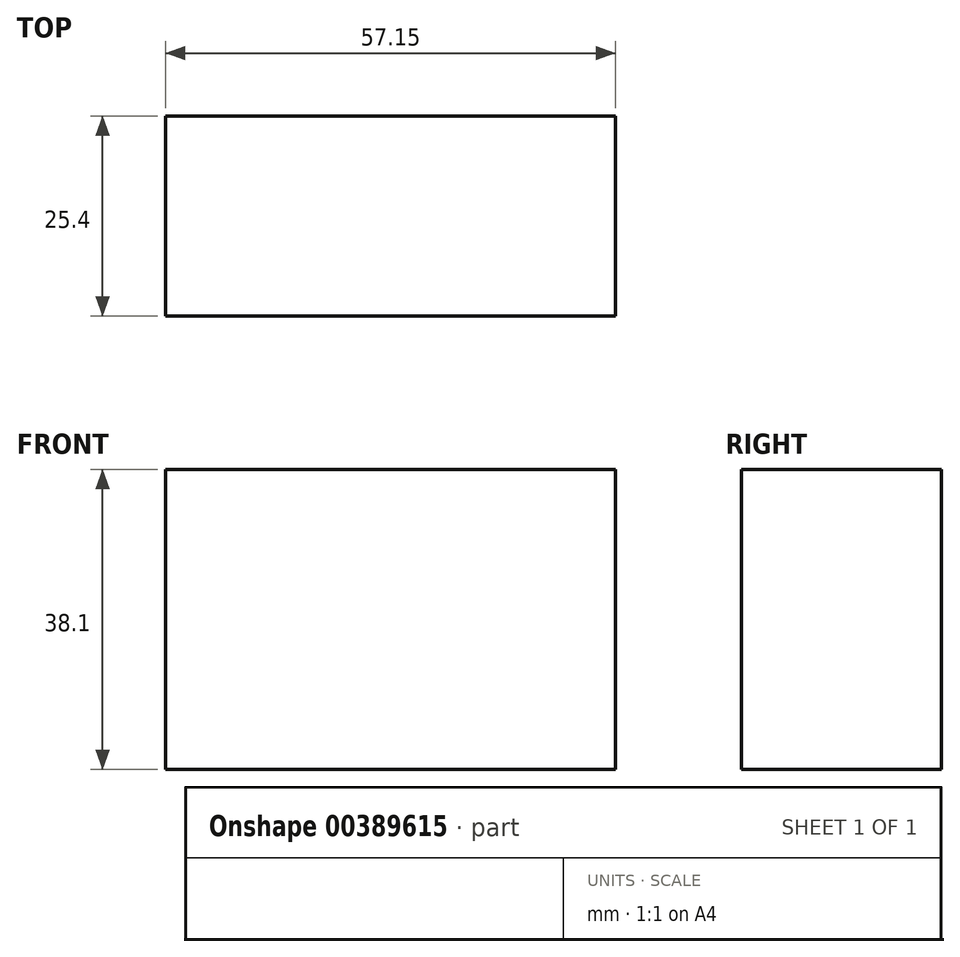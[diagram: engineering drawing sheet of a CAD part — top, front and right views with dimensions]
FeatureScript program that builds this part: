
annotation { "Feature Type Name" : "Feature", "Feature Type Description" : "" }
export const myFeature = defineFeature(function(context is Context, id is Id, definition is map)
    precondition{}
    {
        {
            var Q0;
            Q0=qCreatedBy(makeId("Front.planeOp"),FACE);
            var sketch = newSketch(context, id + "F0", { "sketchPlane" : qUnion([Q0])});
            skLineSegment(sketch, "E0", {"start": v(0, 0) * mm, "end": v(0, 38.1) * mm});
            skLineSegment(sketch, "E1", {"start": v(0, 38.1) * mm, "end": v(57.15, 38.1) * mm});
            skLineSegment(sketch, "E2", {"start": v(57.15, 38.1) * mm, "end": v(57.15, 0) * mm});
            skLineSegment(sketch, "E3", {"start": v(57.15, 0) * mm, "end": v(0, 0) * mm});
            skSolve(sketch);
        }
        {
            var Q0;
            Q0 = qSketchRegion(id + "F0", true);
            extrude(context, id + "F1", {"entities" : qUnion([Q0]), "depth" : 25.4 * mm});
        }
    });
